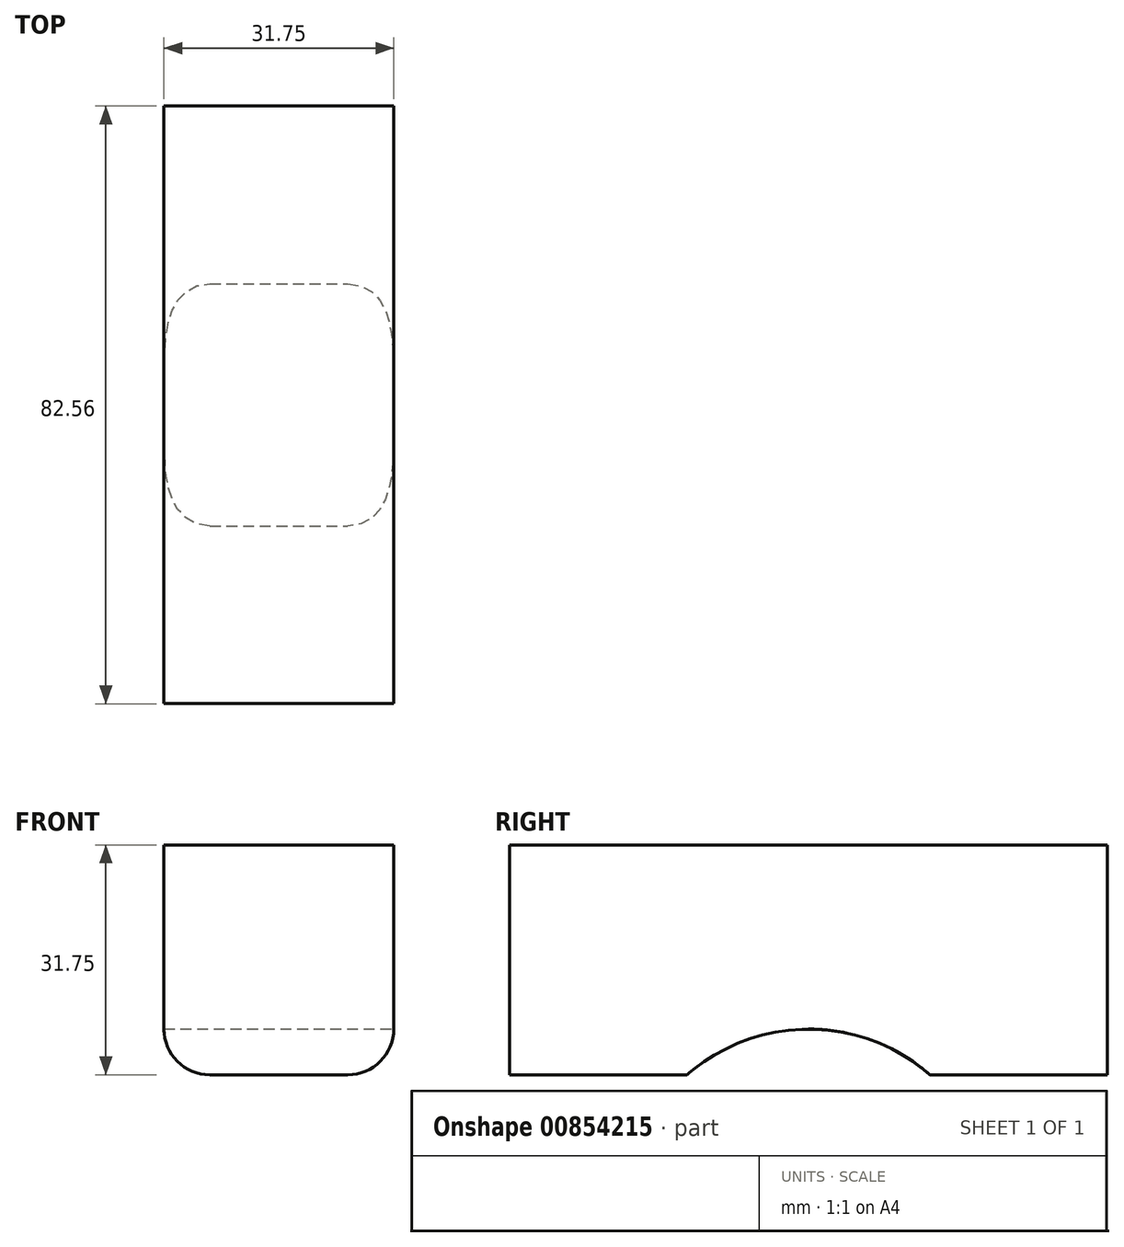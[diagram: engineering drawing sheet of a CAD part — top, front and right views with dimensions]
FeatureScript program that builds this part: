
annotation { "Feature Type Name" : "Feature", "Feature Type Description" : "" }
export const myFeature = defineFeature(function(context is Context, id is Id, definition is map)
    precondition{}
    {
        {
            var Q0;
            Q0=qCreatedBy(makeId("Top.planeOp"),FACE);
            var sketch = newSketch(context, id + "F0", { "sketchPlane" : qUnion([Q0])});
            skLineSegment(sketch, "E0.bottom", {"start": v(0, -41.28) * mm, "end": v(-31.75, -41.28) * mm});
            skLineSegment(sketch, "E0.top", {"start": v(0, 41.28) * mm, "end": v(-31.75, 41.28) * mm});
            skLineSegment(sketch, "E0.left", {"start": v(0, -41.28) * mm, "end": v(0, 41.28) * mm});
            skLineSegment(sketch, "E0.right", {"start": v(-31.75, -41.28) * mm, "end": v(-31.75, 41.28) * mm});
            skPoint(sketch, "E0.middle", {"position": v(-15.88, 0) * mm});
            skSolve(sketch);
        }
        {
            var Q0;
            Q0 = qSketchRegion(id + "F0", true);
            extrude(context, id + "F1", {"entities" : qUnion([Q0]), "depth" : 31.75 * mm, "offsetDistance" : 25.4 * mm});
        }
        {
            var Q0;
            Q0=makeQuery(id+"F1.opExtrude","CAP_EDGE",EDGE,{"disambiguationData":[OSD([sQuery(id+"F0.wireOp",EDGE,"E0.left")])],"isStart":true});
            var Q1;
            Q1=makeQuery(id+"F1.opExtrude","CAP_EDGE",EDGE,{"disambiguationData":[OSD([sQuery(id+"F0.wireOp",EDGE,"E0.right")])],"isStart":true});
            fillet(context, id + "F2", {"entities" : qUnion([Q0, Q1]), "radius" : 6.35 * mm, "tangentPropagation" : true, "allowEdgeOverflow" : false});
        }
        {
            var Q0;
            Q0=makeQuery(id+"F1.opExtrude","SWEPT_FACE",FACE,{"disambiguationData":[OSD([sQuery(id+"F0.wireOp",EDGE,"E0.left")])]});
            var sketch = newSketch(context, id + "F3", { "sketchPlane" : qUnion([Q0])});
            skArc(sketch, "E1", {"start": v(-0.28, 6.3) * mm, "mid": v(-9.3, 4.54) * mm, "end": v(-17.1, -0.32) * mm});
            skLineSegment(sketch, "E2", {"start": v(-17.1, -0.32) * mm, "end": v(-17.1, -0.32) * mm});
            skArc(sketch, "E3", {"start": v(-17.1, -0.32) * mm, "mid": v(9.3, -42.73) * mm, "end": v(-0.28, 6.3) * mm});
            skSolve(sketch);
        }
        {
            var Q0;
            Q0 = qSketchRegion(id + "F3", true);
            extrude(context, id + "F4", {"entities" : qUnion([Q0]), "operationType" : NewBodyOperationType.REMOVE, "oppositeDirection" : true, "depth" : 31.75 * mm, "offsetDistance" : 25.4 * mm});
        }
    });
